# Revit family: KEUCO_14951010000
name_source: partatom
category: Sonderausstattung
revit_build: Autodesk Revit 2016 (Build: 20150220_1215(x64)
units: mm (PartAtom-declared; Revit-internal decimal feet)

## family parameters
Arbeitsebenenbasiert = Nein
Beim Laden mit Abzugskörper schneiden = Nein
Bemaßung runder Anschluss = Durchmesser verwenden
Gemeinsam genutzt = Nein
Immer vertikal = Ja
Raumberechnungspunkt = Nein
Teiletyp = Normal

## types (3) — shared parameters
Beschreibung = komplett mit Halter und Pumpe,
für Flüssigseife
Füllmenge: ca. 280 ml
Dosiermenge: ca. 0,5 ml/Hub
Gewicht = 382
Hersteller = KEUCO
Kategorie = ACC
Preisgruppe = 1
Serie = Plan
URL = https://www.keuco.com
Verwendung = BI / GWC / WP

## per-type parameters (varying)
| type | Ausschreibungstext |
| 14951010000 | KEUCO PLAN Lotionspender 14951010000 
komplett mit Halter und Pumpe,
hochglanzverchromter Halter mit Lotionspender für Flüssigseife,
in ästhetischem, funktionalem Design, leicht zu reinigen, 
komplett mit Halter und Stülpbecher aus Metall, hochglanzverchromt,
Füllmenge ca. 280 ml, Dosiermenge ca. 0,5 ml/Hub,
Höhe 125 mm, Durchmesser 76 mm, Ausladung 101 mm,
der Lotionspender wird verdeckt angebracht,
Lieferung inkl. korrosionsfreiem Befestigungsmaterial |
| 14951070000 | KEUCO PLAN Lotionspender 14951070000 
komplett mit Halter und Pumpe,
Halter aus hochwertigem Edelstahl mit Lotionspender für Flüssigseife,
in ästhetischem, funktionalem Design, leicht zu reinigen, 
komplett mit Halter und Stülpbecher aus Edelstahl,
Füllmenge ca. 280 ml, Dosiermenge ca. 0,5 ml/Hub,
Höhe 125 mm, Durchmesser 76 mm, Ausladung 101 mm,
der Lotionspender wird verdeckt angebracht,
Lieferung inkl. korrosionsfreiem Befestigungsmaterial |
| 14951170000 | KEUCO PLAN Lotionspender 14951170000 
komplett mit Halter und Pumpe,
Halter in Aluminium-Optik mit Lotionspender für Flüssigseife,
in ästhetischem, funktionalem Design, leicht zu reinigen, 
komplett mit Halter und Stülpbecher aus Metall, Aluminium-Optik
Füllmenge ca. 280 ml, Dosiermenge ca. 0,5 ml/Hub,
Höhe 125 mm, Durchmesser 76 mm, Ausladung 101 mm,
der Lotionspender wird verdeckt angebracht,
Lieferung inkl. korrosionsfreiem Befestigungsmaterial |

note: column(s) folded — value = type name in every type: Artikelnummer

## geometry (parser evidence)
native form markers: Blend x2, Sweep x3
no freeform markers — native parametric forms only
